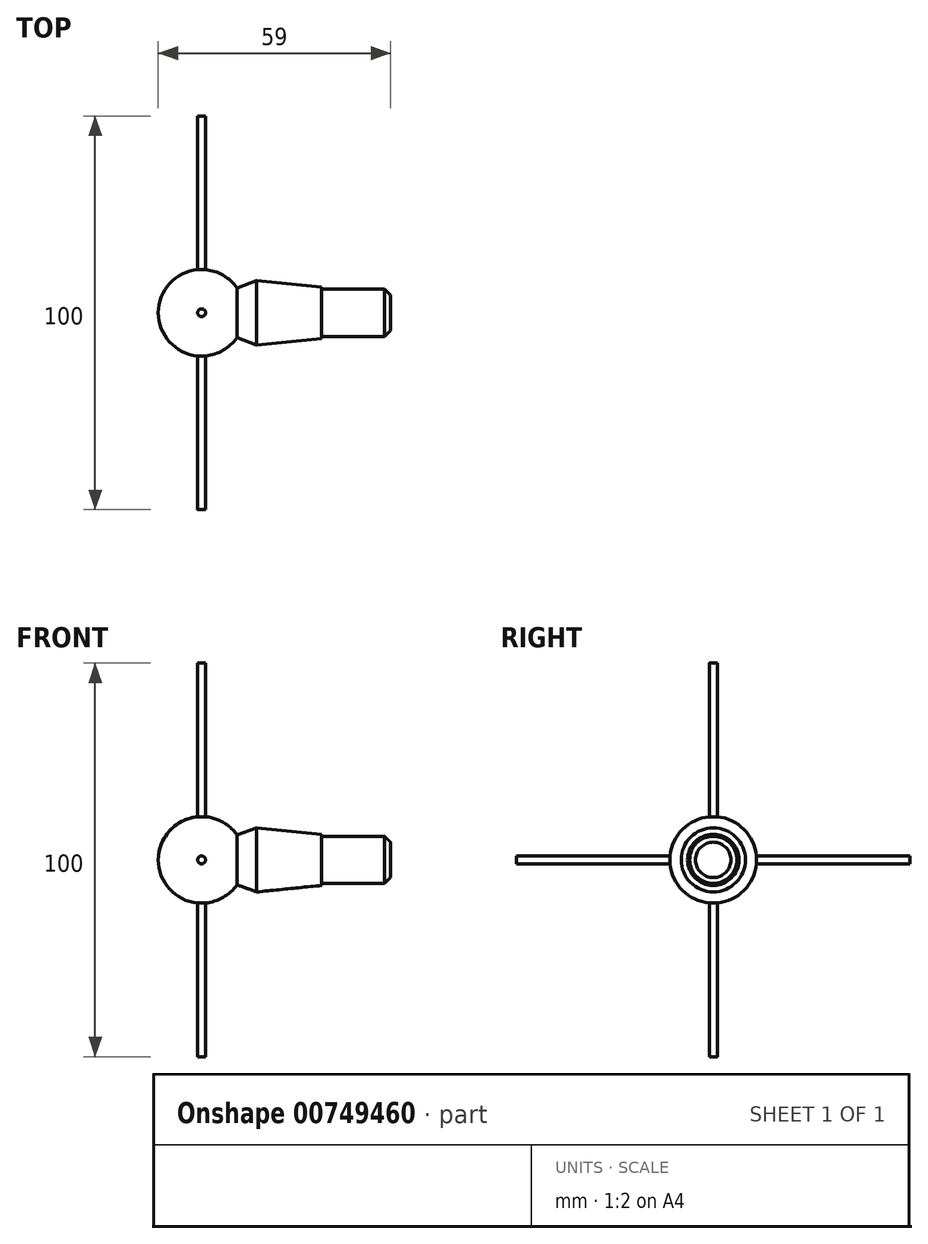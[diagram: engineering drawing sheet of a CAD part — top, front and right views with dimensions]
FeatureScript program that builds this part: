
annotation { "Feature Type Name" : "Feature", "Feature Type Description" : "" }
export const myFeature = defineFeature(function(context is Context, id is Id, definition is map)
    precondition{}
    {
        {
            var Q0;
            Q0=qCreatedBy(makeId("Front.planeOp"),FACE);
            var sketch = newSketch(context, id + "F0", { "sketchPlane" : qUnion([Q0])});
            skArc(sketch, "E0", {"start": v(-11, 0) * mm, "mid": v(-3.32, 10.49) * mm, "end": v(9, 6.33) * mm});
            skLineSegment(sketch, "E1", {"start": v(14, 8.15) * mm, "end": v(30.5, 6.5) * mm});
            skLineSegment(sketch, "E2", {"start": v(30.5, 6.5) * mm, "end": v(30.5, 6) * mm});
            skLineSegment(sketch, "E3", {"start": v(30.5, 6) * mm, "end": v(48, 6) * mm});
            skLineSegment(sketch, "E4", {"start": v(48, 6) * mm, "end": v(48, 0) * mm});
            skLineSegment(sketch, "E5", {"start": v(48, 0) * mm, "end": v(-11, 0) * mm});
            skLineSegment(sketch, "E6", {"start": v(9, 6.33) * mm, "end": v(14, 8.15) * mm});
            skLineSegment(sketch, "E7", {"start": v(0, 0) * mm, "end": v(-22, 0) * mm, "construction": true});
            skSolve(sketch);
        }
        {
            var Q0;
            Q0 = qSketchRegion(id + "F0", true);
            var Q1;
            Q1=sQuery(id+"F0.wireOp",EDGE,"E5");
            revolve(context, id + "F1", {"surfaceOperationType" : NewSurfaceOperationType.NEW, "entities" : qUnion([Q0]), "axis" : qUnion([Q1]), "revolveType" : RevolveType.FULL});
        }
        {
            var Q0;
            Q0=makeQuery(id+"F1.opRevolve","SWEPT_EDGE",EDGE,{"disambiguationData":[OSD([sQuery(id+"F0.wireOp",EDGE,"E3"),sQuery(id+"F0.wireOp",EDGE,"E4")])]});
            chamfer(context, id + "F2", {"entities" : qUnion([Q0]), "width" : 1.5 * mm, "tangentPropagation" : true});
        }
        {
            var Q0;
            Q0=qCreatedBy(makeId("Front.planeOp"),FACE);
            var sketch = newSketch(context, id + "F3", { "sketchPlane" : qUnion([Q0])});
            skCircle(sketch, "E8", {"center": v(0, 0) * mm, "radius": 1 * mm});
            skSolve(sketch);
        }
        {
            var Q0;
            Q0 = qSketchRegion(id + "F3", true);
            extrude(context, id + "F4", {"entities" : qUnion([Q0]), "operationType" : NewBodyOperationType.ADD, "depth" : 100 * mm, "offsetDistance" : 25 * mm, "symmetric" : true});
        }
        {
            var Q0;
            Q0=qCreatedBy(makeId("Top.planeOp"),FACE);
            var sketch = newSketch(context, id + "F5", { "sketchPlane" : qUnion([Q0])});
            skCircle(sketch, "E9", {"center": v(0, 0) * mm, "radius": 1 * mm});
            skSolve(sketch);
        }
        {
            var Q0;
            Q0 = qSketchRegion(id + "F5", true);
            extrude(context, id + "F6", {"entities" : qUnion([Q0]), "operationType" : NewBodyOperationType.ADD, "depth" : 100 * mm, "offsetDistance" : 25 * mm, "symmetric" : true});
        }
    });
